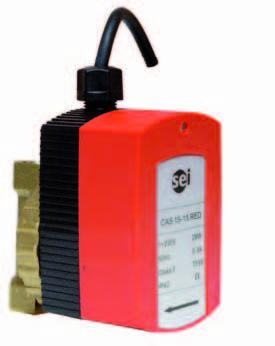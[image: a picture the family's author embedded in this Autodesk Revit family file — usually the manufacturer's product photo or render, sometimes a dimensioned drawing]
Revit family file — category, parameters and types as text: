
# Revit family: CAS_15-15Red-AC52155
name_source: partatom
category: Aparatos eléctricos
revit_build: Autodesk Revit 2016 (Build: 20150220_1215(x64)
units: mm (PartAtom-declared; Revit-internal decimal feet)

## family parameters
Compartido = No
Corte con vacíos al cargar = No
Cota de conector redondo = Diámetro de uso
Mantener orientación de anotación = No
Número OmniClass = 23.80.00.00
Punto de cálculo de habitación = No
Se basa en plano de trabajo = No
Siempre vertical = Sí
Tipo de pieza = Caja de conexiones
Título OmniClass = Electric Power and Lighting

## types (2) — shared parameters
Fabricante = SALVADOR ESCODA
URL = www.salvadorescoda.com
zero-valued in all types: Costo

## per-type parameters (varying)
| type | Aislamiento | Caudal | Código de montaje | Descripción | Dimensiones Unidad Interior | Imagen de tipo | Intensidad máx. | Modelo | Motor | Máx. presión trabajo | Máxima dureza del agua | Peso | Potencia máx | Presión disponible | Presión mínima aspiración | Protección | Rango temperatura agua | Regulable | Temperatura ambiente |
| MVD-22T2 | 35 dB(A) |  | CL23370 | CONDUCTO BAJA SILUETA | 700 x 210 x 500 mm | <Ninguno> |  | MVD-22T2/DHN1-DA5 | 521 m3/h | 2,2kW / 39W |  | 17,5 kg neto |  |  |  | 6,35 mm (1/4") | 2,6kW / 39W |  | DC / WZDK100-38GS |
| CAS-Red | Clase F | 0,2 m3/h | AC52156 | BOMBA CIRCULADORA PARA ACS | 115 x 75 x 95 mm | SEI_CAS_RED.jpg | 0,3 A | CAS 15-15 RED | 2 polos, 1x230V - 50Hz | 10 bar | 35 ºF (TH) | 2,9 Kgs | 23 W | 1 m.c.a. | 0,2 bar | IP 42 | 2º a 95 ºC | 3 velocidades | Hasta 40ºC |
